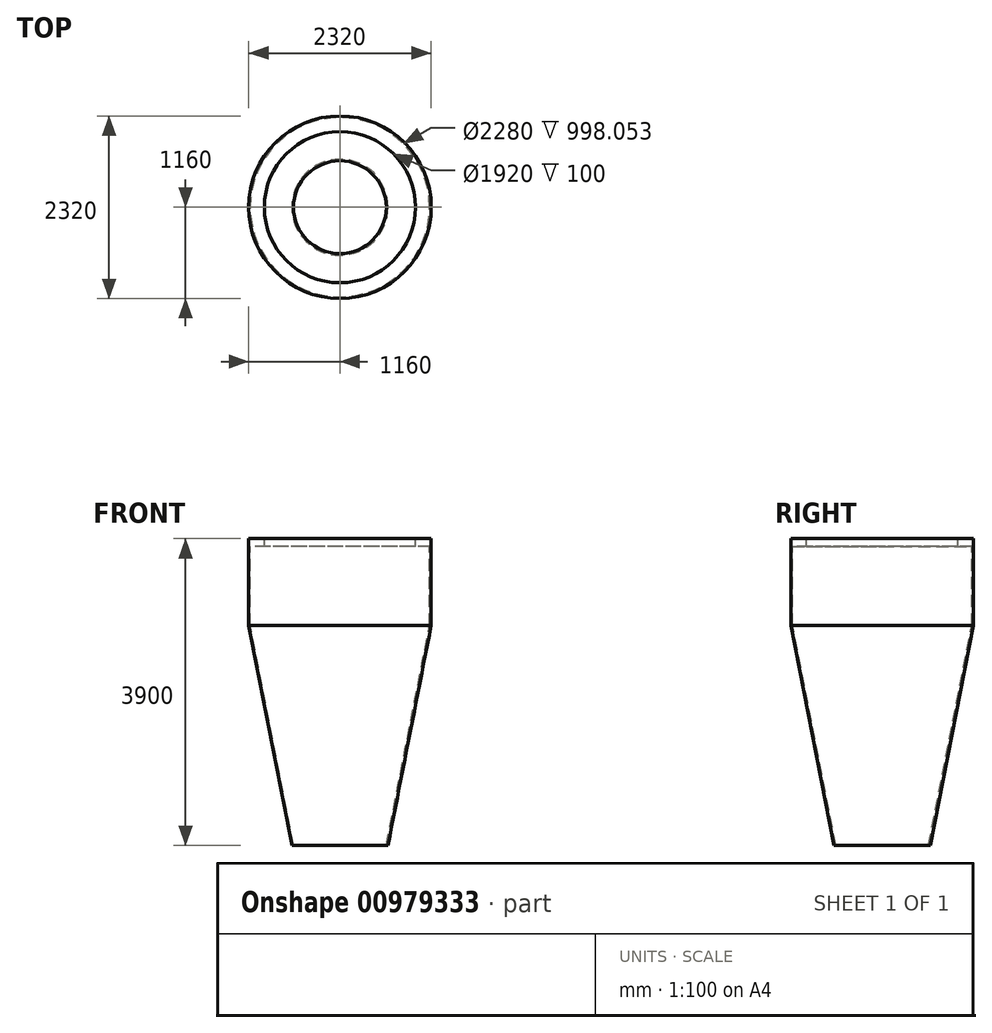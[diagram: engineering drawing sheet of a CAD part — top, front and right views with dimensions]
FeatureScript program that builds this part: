
annotation { "Feature Type Name" : "Feature", "Feature Type Description" : "" }
export const myFeature = defineFeature(function(context is Context, id is Id, definition is map)
    precondition{}
    {
        {
            var Q0;
            Q0=qCreatedBy(makeId("Front.planeOp"),FACE);
            var sketch = newSketch(context, id + "F0", { "sketchPlane" : qUnion([Q0])});
            skLineSegment(sketch, "E0.bottom", {"start": v(-1160, 100) * mm, "end": v(-960, 100) * mm});
            skLineSegment(sketch, "E0.top", {"start": v(-1160, 0) * mm, "end": v(-960, 0) * mm});
            skLineSegment(sketch, "E0.left", {"start": v(-1160, 100) * mm, "end": v(-1160, 0) * mm});
            skLineSegment(sketch, "E0.right", {"start": v(-960, 100) * mm, "end": v(-960, 0) * mm});
            skLineSegment(sketch, "E1", {"start": v(0, 0) * mm, "end": v(0, -411.57) * mm, "construction": true});
            skLineSegment(sketch, "E2", {"start": v(-1160, 0) * mm, "end": v(-1160, -1000) * mm});
            skLineSegment(sketch, "E3", {"start": v(-1160, -1000) * mm, "end": v(-609.5, -3800) * mm});
            skLineSegment(sketch, "E4", {"start": v(-609.5, -3800) * mm, "end": v(-589.88, -3796.14) * mm});
            skLineSegment(sketch, "E5", {"start": v(-589.88, -3796.14) * mm, "end": v(-1140, -998.05) * mm});
            skLineSegment(sketch, "E6", {"start": v(-1140, -998.05) * mm, "end": v(-1140, 0) * mm});
            skLineSegment(sketch, "E7", {"start": v(-1140, 0) * mm, "end": v(-1160, 0) * mm});
            skSolve(sketch);
        }
        {
            var Q0;
            Q0=makeQuery(id+"F0.imprint","IMPRINT",FACE,{"disambiguationData":[TD([[makeQuery(id+"F0.imprint","IMPRINT",EDGE,{"derivedFrom":sQuery(id+"F0.wireOp",EDGE,"E0.bottom")}),-1.0]])]});
            var Q1;
            Q1=makeQuery(id+"F0.imprint","IMPRINT",FACE,{"disambiguationData":[TD([[makeQuery(id+"F0.imprint","IMPRINT",EDGE,{"derivedFrom":sQuery(id+"F0.wireOp",EDGE,"E2")}),1.0]])]});
            var Q2;
            Q2=sQuery(id+"F0.wireOp",EDGE,"E1");
            revolve(context, id + "F1", {"surfaceOperationType" : NewSurfaceOperationType.NEW, "entities" : qUnion([Q0, Q1]), "axis" : qUnion([Q2]), "revolveType" : RevolveType.FULL});
        }
    });
